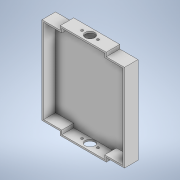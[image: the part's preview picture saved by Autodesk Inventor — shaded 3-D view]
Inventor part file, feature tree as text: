
AUTODESK INVENTOR PART (.ipt)
format: ipt  version: 2022.1 (Build 261234000, 234)  size: 174,080 bytes
history: native  units: mm
features: extrude x3, sketch x3
ambient origin geometry x8: Origin, YZ Plane, XZ Plane, XY Plane, X Axis, Y Axis, Z Axis, Center Point
bodies: Solid1 (feature_tree)
feature tree (6):
  extrude  "Extrusion1"  Depth=120.0mm
  extrude  "Extrusion2"  Depth=2.0mm
  extrude  "Extrusion4"  Depth=2.0mm
  sketch  "Sketch1"  dims[d0=58.0mm d1=120.0mm]
  sketch  "Sketch2"  dims[d2=2.0mm d3=0.0mm d4=2.0mm]
  sketch  "Sketch6"  dims[d5=2.0mm d6=2.0mm d7=2.0mm d8=15.0mm d9=0.0mm d20=23.0mm d21=5.0mm d22=5.0mm d26=23.0mm d27=5.0mm d28=5.0mm d30=2.0mm d31=2.0mm d32=2.0mm d33=2.0mm d34=2.0mm d35=2.0mm d46=12.0mm d47=3.0mm d48=3.0mm d49=10.0mm d50=10.0mm d51=8.5mm d52=8.5mm d53=8.5mm d54=58.0mm d55=29.0mm d56=10.0mm d57=0.0mm]
